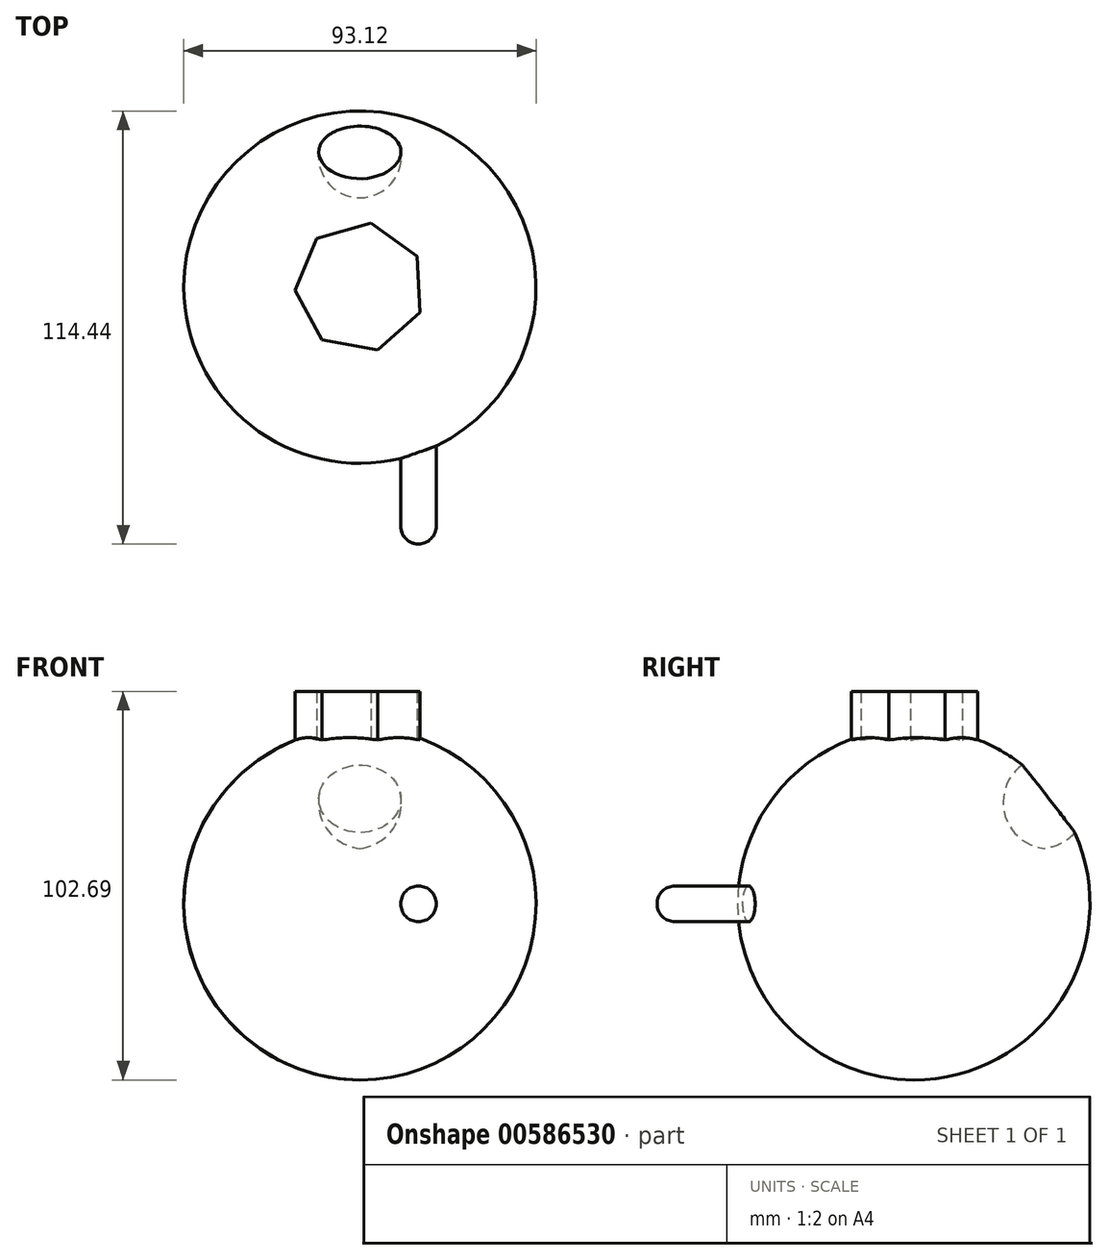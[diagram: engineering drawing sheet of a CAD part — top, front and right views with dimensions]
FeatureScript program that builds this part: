
annotation { "Feature Type Name" : "Feature", "Feature Type Description" : "" }
export const myFeature = defineFeature(function(context is Context, id is Id, definition is map)
    precondition{}
    {
        {
            var Q0;
            Q0=qCreatedBy(makeId("Front.planeOp"),FACE);
            var sketch = newSketch(context, id + "F0", { "sketchPlane" : qUnion([Q0])});
            skCircle(sketch, "E0", {"center": v(0, 0) * mm, "radius": 46.56 * mm});
            skLineSegment(sketch, "E1", {"start": v(0, 46.56) * mm, "end": v(0, -55.93) * mm});
            skSolve(sketch);
        }
        {
            var Q0;
            {var subQ0=sQuery(id+"F0.wireOp",EDGE,"E1");var subQ1=sQuery(id+"F0.wireOp",EDGE,"E0");var subQ2=makeQuery(id+"F0.imprint","INTERSECT",VERTEX,{"disambiguationData":[OD(0.0)],"derivedFrom":[subQ1,subQ0]});Q0=makeQuery(id+"F0.imprint","IMPRINT",FACE,{"disambiguationData":[TD([[makeQuery(id+"F0.imprint","IMPRINT",EDGE,{"disambiguationData":[TD([[subQ2,-1.0]])],"derivedFrom":subQ1}),1.0]])]});}
            var Q1;
            Q1=sQuery(id+"F0.wireOp",EDGE,"E1");
            revolve(context, id + "F1", {"entities" : qUnion([Q0]), "axis" : qUnion([Q1]), "revolveType" : RevolveType.FULL});
        }
        {
            var Q0;
            Q0=qCreatedBy(makeId("Right.planeOp"),FACE);
            var sketch = newSketch(context, id + "F2", { "sketchPlane" : qUnion([Q0])});
            skLineSegment(sketch, "E2", {"start": v(34.57, 38.92) * mm, "end": v(34.57, 14.66) * mm});
            skArc(sketch, "E3", {"start": v(34.57, 38.92) * mm, "mid": v(23.61, 26.8) * mm, "end": v(34.57, 14.66) * mm});
            skSolve(sketch);
        }
        {
            var Q0;
            Q0 = qSketchRegion(id + "F2", true);
            var Q1;
            Q1=sQuery(id+"F2.wireOp",EDGE,"E2");
            revolve(context, id + "F3", {"operationType" : NewBodyOperationType.REMOVE, "entities" : qUnion([Q0]), "axis" : qUnion([Q1]), "revolveType" : RevolveType.FULL, "oppositeDirection" : true});
        }
        {
            var Q0;
            Q0=qCreatedBy(makeId("Top.planeOp"),FACE);
            var sketch = newSketch(context, id + "F4", { "sketchPlane" : qUnion([Q0])});
            skCircle(sketch, "E4.cCircle", {"center": v(0, 0) * mm, "radius": 15.47 * mm, "construction": true});
            skLineSegment(sketch, "E4.0", {"start": v(-10, -13.96) * mm, "end": v(-17.15, -0.88) * mm});
            skLineSegment(sketch, "E4.1", {"start": v(-17.15, -0.88) * mm, "end": v(-11.38, 12.86) * mm});
            skLineSegment(sketch, "E4.2", {"start": v(-11.38, 12.86) * mm, "end": v(2.95, 16.92) * mm});
            skLineSegment(sketch, "E4.3", {"start": v(2.95, 16.92) * mm, "end": v(15.07, 8.24) * mm});
            skLineSegment(sketch, "E4.4", {"start": v(15.07, 8.24) * mm, "end": v(15.84, -6.65) * mm});
            skLineSegment(sketch, "E4.5", {"start": v(15.84, -6.65) * mm, "end": v(4.68, -16.52) * mm});
            skLineSegment(sketch, "E4.6", {"start": v(4.68, -16.52) * mm, "end": v(-10, -13.96) * mm});
            skPoint(sketch, "E4.0.midPoint", {"position": v(-13.58, -7.42) * mm});
            skSolve(sketch);
        }
        {
            var Q0;
            Q0 = qSketchRegion(id + "F4", true);
            extrude(context, id + "F5", {"entities" : qUnion([Q0]), "operationType" : NewBodyOperationType.ADD, "depth" : 56.13 * mm, "offsetDistance" : 25.4 * mm});
        }
        {
            var Q0;
            Q0=qCreatedBy(makeId("Top.planeOp"),FACE);
            var sketch = newSketch(context, id + "F6", { "sketchPlane" : qUnion([Q0])});
            skLineSegment(sketch, "E5", {"start": v(20.2, -30.23) * mm, "end": v(20.2, -63.18) * mm});
            skLineSegment(sketch, "E6", {"start": v(20.2, -30.23) * mm, "end": v(10.78, -30.23) * mm});
            skLineSegment(sketch, "E7", {"start": v(10.78, -30.23) * mm, "end": v(10.78, -63.18) * mm});
            skArc(sketch, "E8", {"start": v(10.78, -63.18) * mm, "mid": v(15.5, -67.88) * mm, "end": v(20.2, -63.18) * mm});
            skLineSegment(sketch, "E9", {"start": v(15.5, -67.88) * mm, "end": v(15.5, -30.23) * mm});
            skSolve(sketch);
        }
        {
            var Q0;
            {var subQ0=sQuery(id+"F6.wireOp",EDGE,"E5");Q0=makeQuery(id+"F6.imprint","IMPRINT",FACE,{"disambiguationData":[TD([[makeQuery(id+"F6.imprint","IMPRINT",EDGE,{"derivedFrom":subQ0}),-1.0]])]});}
            var Q1;
            Q1=sQuery(id+"F6.wireOp",EDGE,"E9");
            revolve(context, id + "F7", {"operationType" : NewBodyOperationType.ADD, "entities" : qUnion([Q0]), "axis" : qUnion([Q1]), "revolveType" : RevolveType.FULL});
        }
    });
